# Revit family: BTKP
name_source: partatom
category: Leuchten
revit_build: Autodesk Revit 2017 (Build: 20160225_1515(x64)
units: mm (PartAtom-declared; Revit-internal decimal feet)

## family parameters
Basisbauteil = Fläche
Beim Laden mit Abzugskörper schneiden = Nein
Bemaßung runder Anschluss = Durchmesser verwenden
Gemeinsam genutzt = Nein
Lichtquelle = Ja
OmniClass-Nummer = 23.80.70.11
OmniClass-Titel = Luminaries for Internal Lighting
Raumberechnungspunkt = Nein
Teiletyp = Normal

## types (16) — shared parameters
Beschreibung = Suspended luminaire
Body = RAL 9003
Certification = CE
Cover = RIDI Light Emitting Surface
Emissionsform beim Rendern sichtbar = Nein
Energy Class = A++ - A
Farbfilter = 16777215
Farbtemperaturverschiebung bei Dämpfen der Lampe = <Keine Auswahl>
Hersteller = Spectral
IP Rating = IP 20
Lampe = LED-Modul
Neigungswinkel = -90.00°
Number of Poles = 1
Suspension = RIDI Metall silver 9006
Voltage = 230 V
Von Länge des Rechtecks aussenden = 38 mm
Width = 42 mm  [stored 0.137795 ft]
zero-valued in all types: Vorgabe-Ansicht

## per-type parameters (varying)
| type | Datei für fotometrisches Netz | Height | Length | Modell | Scheinlast | Suspension Distance | Von Breite des Rechtecks ausssenden | Weight |
| BTKP 120X20/400-840 DPO-SWF | BTKP 120x20_400-840 DPO-SWF.IES | 200 mm  [stored 0.656168 ft] | 1200 mm | SPK0620014BL
SPK0620014BL
SPK0620014BL
SPK0620014BL
SPK0620014BL
SPK0620014BL | 27 VA | 800 mm | 1196 mm | 7.2 kg |
| BTKP 120X20/400-840 MPS-SWF | BTKP 120_400-840 MPS.IES | 200 mm  [stored 0.656168 ft] | 1200 mm | SPK0620015BL | 27 VA | 800 mm | 1196 mm | 7.2 kg |
| BTKP 120X20/400-840 DPO-DA-SWF | BTKP 120x20_400-840 DPO-SWF.IES | 200 mm  [stored 0.656168 ft] | 1200 mm | SPK0630014BL
SPK0620014BL
SPK0620014BL
SPK0620014BL
SPK0620014BL
SPK0620014BL | 27 VA | 800 mm | 1196 mm | 7.2 kg |
| BTKP 120X20/400-840 MPS-DA-SWF | BTKP 120_400-840 MPS.IES | 200 mm  [stored 0.656168 ft] | 1200 mm | SPK0630015BL | 27 VA | 800 mm | 1196 mm | 7.2 kg |
| BTKP 120X30/400-840 DPO-DA-SWF | BTKP 120x20_400-840 DPO-SWF.IES | 300 mm | 1200 mm | SPK0630019BL | 27 VA | 800 mm | 1196 mm | 8.9 kg |
| BTKP 120X30/400-840 DPO-SWF | BTKP 120x20_400-840 DPO-SWF.IES | 300 mm | 1200 mm | SPK0620019BL | 27 VA | 800 mm | 1196 mm | 8.9 kg |
| BTKP 120X30/400-840 MPS-DA-SWF | BTKP 120_400-840 MPS.IES | 300 mm | 1200 mm | SPK0630018BL | 27 VA | 800 mm | 1196 mm | 8.9 kg |
| BTKP 120X30/400-840 MPS-SWF | BTKP 120_400-840 MPS.IES | 300 mm | 1200 mm | SPK0620018BL | 27 VA | 800 mm | 1196 mm | 8.9 kg |
| BTKP 150X20/500-840 DPO-DA-SWF | BTKP 120x20_400-840 DPO-SWF.IES | 200 mm  [stored 0.656168 ft] | 1500 mm  [stored 4.92126 ft] | SPK0630022BL | 33 VA | 1100 mm | 1496 mm | 8.7 kg |
| BTKP 150X20/500-840 DPO-SWF | BTKP 120x20_400-840 DPO-SWF.IES | 200 mm  [stored 0.656168 ft] | 1500 mm  [stored 4.92126 ft] | SPK0620022BL | 33 VA | 1100 mm | 1496 mm | 8.7 kg |
| BTKP 150X20/500-840 MPS-DA-SWF | BTKP 120_400-840 MPS.IES | 200 mm  [stored 0.656168 ft] | 1500 mm  [stored 4.92126 ft] | SPK0630023BL | 33 VA | 1100 mm | 1496 mm | 8.7 kg |
| BTKP 150X20/500-840 MPS-SWF | BTKP 120_400-840 MPS.IES | 200 mm  [stored 0.656168 ft] | 1500 mm  [stored 4.92126 ft] | SPK0620023BL | 33 VA | 1100 mm | 1496 mm | 8.7 kg |
| BTKP 150X30/500-840 DPO-DA-SWF | BTKP 120x20_400-840 DPO-SWF.IES | 300 mm | 1500 mm  [stored 4.92126 ft] | SPK0630026BL | 33 VA | 1100 mm | 1496 mm | 10.8 kg |
| BTKP 150X30/500-840 DPO-SWF | BTKP 120x20_400-840 DPO-SWF.IES | 300 mm | 1500 mm  [stored 4.92126 ft] | SPK0620026BL | 33 VA | 1100 mm | 1496 mm | 10.8 kg |
| BTKP 150X30/500-840 MPS-DA-SWF | BTKP 120_400-840 MPS.IES | 300 mm | 1500 mm  [stored 4.92126 ft] | SPK0630027BL | 33 VA | 1100 mm | 1496 mm | 10.8 kg |
| BTKP 150X30/500-840 MPS-SWF | BTKP 120_400-840 MPS.IES | 300 mm | 1500 mm  [stored 4.92126 ft] | SPK0620027BL | 33 VA | 1100 mm | 1496 mm | 10.8 kg |

note: [stored X ft] marks values corroborated as IEEE doubles in the binary element streams (Revit-internal decimal feet)

## geometry (parser evidence)
native form markers: Sweep x3
no freeform markers — native parametric forms only
